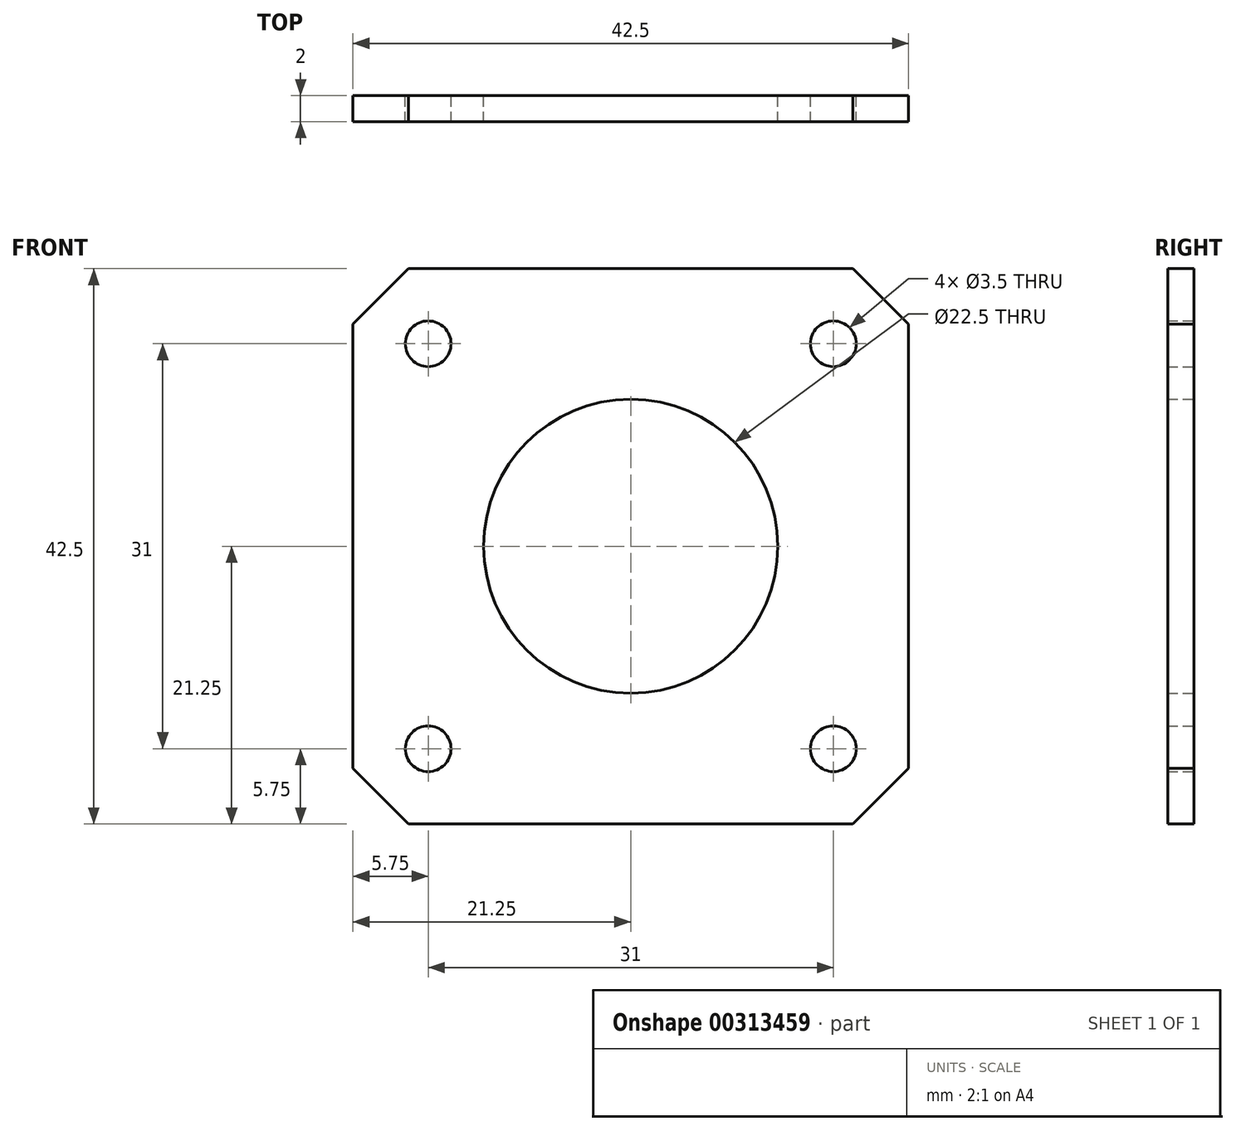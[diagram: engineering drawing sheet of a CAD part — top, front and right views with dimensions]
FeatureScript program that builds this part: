
annotation { "Feature Type Name" : "Feature", "Feature Type Description" : "" }
export const myFeature = defineFeature(function(context is Context, id is Id, definition is map)
    precondition{}
    {
        {
            var Q0;
            Q0=qCreatedBy(makeId("Front.planeOp"),FACE);
            var sketch = newSketch(context, id + "F0", { "sketchPlane" : qUnion([Q0])});
            skCircle(sketch, "E0", {"center": v(0, 0) * mm, "radius": 11.25 * mm});
            skLineSegment(sketch, "E1.bottom", {"start": v(-21.25, -21.25) * mm, "end": v(21.25, -21.25) * mm});
            skLineSegment(sketch, "E1.top", {"start": v(-21.25, 21.25) * mm, "end": v(21.25, 21.25) * mm});
            skLineSegment(sketch, "E1.left", {"start": v(-21.25, -21.25) * mm, "end": v(-21.25, 21.25) * mm});
            skLineSegment(sketch, "E1.right", {"start": v(21.25, -21.25) * mm, "end": v(21.25, 21.25) * mm});
            skLineSegment(sketch, "E2", {"start": v(-21.25, 0) * mm, "end": v(21.25, 0) * mm, "construction": true});
            skLineSegment(sketch, "E3", {"start": v(0, 21.25) * mm, "end": v(0, -21.25) * mm, "construction": true});
            skCircle(sketch, "E4", {"center": v(-15.5, -15.5) * mm, "radius": 1.75 * mm});
            skCircle(sketch, "E5.0.1.0", {"center": v(-15.5, 15.5) * mm, "radius": 1.75 * mm});
            skCircle(sketch, "E5.1.0.0", {"center": v(15.5, -15.5) * mm, "radius": 1.75 * mm});
            skCircle(sketch, "E5.1.1.0", {"center": v(15.5, 15.5) * mm, "radius": 1.75 * mm});
            skLineSegment(sketch, "E5.direction1", {"start": v(-15.5, -15.5) * mm, "end": v(15.5, -15.5) * mm, "construction": true});
            skLineSegment(sketch, "E5.direction2", {"start": v(-15.5, -15.5) * mm, "end": v(-15.5, 15.5) * mm, "construction": true});
            skSolve(sketch);
        }
        {
            var Q0;
            Q0=makeQuery(id+"F0.imprint","IMPRINT",FACE,{"disambiguationData":[TD([[makeQuery(id+"F0.imprint","IMPRINT",EDGE,{"derivedFrom":sQuery(id+"F0.wireOp",EDGE,"E0")}),-1.0]])]});
            extrude(context, id + "F1", {"entities" : qUnion([Q0]), "depth" : 2 * mm});
        }
        {
            var Q0;
            Q0=makeQuery(id+"F1.opExtrude","CAP_FACE",FACE,{"disambiguationData":[OSD([sQuery(id+"F0.wireOp",EDGE,"E0"),sQuery(id+"F0.wireOp",EDGE,"E1.bottom"),sQuery(id+"F0.wireOp",EDGE,"E1.top"),sQuery(id+"F0.wireOp",EDGE,"E1.left"),sQuery(id+"F0.wireOp",EDGE,"E1.right"),sQuery(id+"F0.wireOp",EDGE,"E4"),sQuery(id+"F0.wireOp",EDGE,"E5.0.1.0"),sQuery(id+"F0.wireOp",EDGE,"E5.1.0.0"),sQuery(id+"F0.wireOp",EDGE,"E5.1.1.0")])],"isStart":false});
            var sketch = newSketch(context, id + "F2", { "sketchPlane" : qUnion([Q0])});
            skLineSegment(sketch, "E6", {"start": v(-21.25, -21.25) * mm, "end": v(-17, -21.25) * mm});
            skLineSegment(sketch, "E7", {"start": v(-17, -21.25) * mm, "end": v(-21.25, -17) * mm});
            skLineSegment(sketch, "E8", {"start": v(-21.25, -17) * mm, "end": v(-21.25, -21.25) * mm});
            skLineSegment(sketch, "E9", {"start": v(21.25, -21.25) * mm, "end": v(17, -21.25) * mm});
            skLineSegment(sketch, "E10", {"start": v(17, -21.25) * mm, "end": v(21.25, -17) * mm});
            skLineSegment(sketch, "E11", {"start": v(21.25, -17) * mm, "end": v(21.25, -21.25) * mm});
            skLineSegment(sketch, "E12", {"start": v(21.25, 21.25) * mm, "end": v(17, 21.25) * mm});
            skLineSegment(sketch, "E13", {"start": v(17, 21.25) * mm, "end": v(21.25, 17) * mm});
            skLineSegment(sketch, "E14", {"start": v(21.25, 17) * mm, "end": v(21.25, 21.25) * mm});
            skLineSegment(sketch, "E15", {"start": v(-21.25, 21.25) * mm, "end": v(-17, 21.25) * mm});
            skLineSegment(sketch, "E16", {"start": v(-17, 21.25) * mm, "end": v(-21.25, 17) * mm});
            skLineSegment(sketch, "E17", {"start": v(-21.25, 17) * mm, "end": v(-21.25, 21.25) * mm});
            skSolve(sketch);
        }
        {
            var Q0;
            Q0=makeQuery(id+"F2.imprint","IMPRINT",FACE,{"disambiguationData":[TD([[makeQuery(id+"F2.imprint","IMPRINT",EDGE,{"derivedFrom":sQuery(id+"F2.wireOp",EDGE,"E15")}),-1.0]])]});
            var Q1;
            Q1=makeQuery(id+"F2.imprint","IMPRINT",FACE,{"disambiguationData":[TD([[makeQuery(id+"F2.imprint","IMPRINT",EDGE,{"derivedFrom":sQuery(id+"F2.wireOp",EDGE,"E12")}),-1.0]])]});
            var Q2;
            Q2=makeQuery(id+"F2.imprint","IMPRINT",FACE,{"disambiguationData":[TD([[makeQuery(id+"F2.imprint","IMPRINT",EDGE,{"derivedFrom":sQuery(id+"F2.wireOp",EDGE,"E9")}),1.0]])]});
            var Q3;
            Q3=makeQuery(id+"F2.imprint","IMPRINT",FACE,{"disambiguationData":[TD([[makeQuery(id+"F2.imprint","IMPRINT",EDGE,{"derivedFrom":sQuery(id+"F2.wireOp",EDGE,"E6")}),1.0]])]});
            var Q4;
            Q4=makeQuery(id+"F1.opExtrude","CAP_FACE",FACE,{"disambiguationData":[OSD([sQuery(id+"F0.wireOp",EDGE,"E0"),sQuery(id+"F0.wireOp",EDGE,"E1.bottom"),sQuery(id+"F0.wireOp",EDGE,"E1.top"),sQuery(id+"F0.wireOp",EDGE,"E1.left"),sQuery(id+"F0.wireOp",EDGE,"E1.right"),sQuery(id+"F0.wireOp",EDGE,"E4"),sQuery(id+"F0.wireOp",EDGE,"E5.0.1.0"),sQuery(id+"F0.wireOp",EDGE,"E5.1.0.0"),sQuery(id+"F0.wireOp",EDGE,"E5.1.1.0")])],"isStart":true});
            var Q5;
            Q5=makeQuery(id+"F1.opExtrude","SWEPT_BODY",BODY,{"disambiguationData":[OSD([sQuery(id+"F0.wireOp",EDGE,"E0"),sQuery(id+"F0.wireOp",EDGE,"E1.bottom"),sQuery(id+"F0.wireOp",EDGE,"E1.top"),sQuery(id+"F0.wireOp",EDGE,"E1.left"),sQuery(id+"F0.wireOp",EDGE,"E1.right"),sQuery(id+"F0.wireOp",EDGE,"E4"),sQuery(id+"F0.wireOp",EDGE,"E5.0.1.0"),sQuery(id+"F0.wireOp",EDGE,"E5.1.0.0"),sQuery(id+"F0.wireOp",EDGE,"E5.1.1.0")])]});
            extrude(context, id + "F3", {"entities" : qUnion([Q0, Q1, Q2, Q3]), "operationType" : NewBodyOperationType.REMOVE, "endBound" : BoundingType.UP_TO_SURFACE, "oppositeDirection" : true, "endBoundEntityFace" : qUnion([Q4]), "endBoundEntityBody" : qUnion([Q5]), "depth" : 25 * mm});
        }
    });
